# Revit family: 220-45 Heavy Retract roof, Retract Frame 3 Sides, Blades Retracting to one side)
name_source: partatom
category: Generic Models
revit_build: Autodesk Revit 2018 (Build: 20190510_1515(x64)
units: mm (PartAtom-declared; Revit-internal decimal feet)

## family parameters
Always vertical = Yes
Can host rebar = No
Cut with Voids When Loaded = No
Part Type = Normal
Room Calculation Point = No
Round Connector Dimension = Use Diameter
Shared = No
Work Plane-Based = No

## types (1)
- 220-45 Heavy Retract roof, Retract Frame 3 Sides, Blades Retracting to one side)
    220-45 HEAYV BLADE AND END CAP = PC COLOUR
    A = 4152 mm
    ANGLE INPUT = 0.00°
    ANGLE LIMIT = 90.00°
    BLADE ANGLE = 0.00°
    BLADE PITCH = 0.83°
    BLADES SPACING = 0 mm  [stored 0 ft]
    BOX SECTION HEIGHT = 300 mm  [stored 0.984252 ft]
    BOX SECTION HEIGHT INPUT = 300 mm  [stored 0.984252 ft]
    BOX SECTION THICKNESS = 3 mm  [stored 0.00984252 ft]
    BOX SECTION THICKNESS INPUT = 3 mm  [stored 0.00984252 ft]
    BOX SECTION WIDTH = 50 mm  [stored 0.164042 ft]
    BOX SECTION WIDTH INPUT = 50 mm  [stored 0.164042 ft]
    DETAIL OFFSET = 0 mm  [stored 0 ft]
    DETAIL OFFSET INPUT = 0 mm  [stored 0 ft]
    FLASHIGN INPUT 2 = 15 mm  [stored 0.0492126 ft]
    FLASHING INPUT = 0 mm  [stored 0 ft]
    GUTTER = PC COLOUR
    GUTTER LENGTH = 4408 mm
    HEIGHT = 2800 mm  [stored 9.18635 ft]
    HEIGHT LIMIT = 2800 mm  [stored 9.18635 ft]
    M1 = 170 mm  [stored 0.557743 ft]
    MODULAR PIVOT SIZE = 4417 mm  [stored 14.4915 ft]
    NUMBER OF BLADES = 20
    O = 60 mm  [stored 0.19685 ft]
    PIVOT = 4500 mm  [stored 14.7638 ft]
    POST = PC COLOUR
    POST LENGTH AND WIDTH SIZE = 100 mm  [stored 0.328084 ft]
    POST LENGTH AND WIDTH SIZE INPUT = 100 mm  [stored 0.328084 ft]
    POST OFFSET = 2500 mm  [stored 8.2021 ft]
    POST OFFSET INPUT = 2500 mm  [stored 8.2021 ft]
    POST THICKNESS = 3 mm  [stored 0.00984252 ft]
    POST THICKNESS INPUT = 3 mm  [stored 0.00984252 ft]
    RETRACT FRAME = PC COLOUR
    SPACING INPUT = 60 mm  [stored 0.19685 ft]
    SPAN = 4500 mm  [stored 14.7638 ft]
    SPAN INPUT = 4500 mm  [stored 14.7638 ft]
    STACKED INPUT = 259 mm  [stored 0.849738 ft]
    WOOL PILE = WOOL pILE

note: [stored X ft] marks values corroborated as IEEE doubles in the binary element streams (Revit-internal decimal feet)

## geometry (parser evidence)
native form markers: Sweep x36
no freeform markers — native parametric forms only
